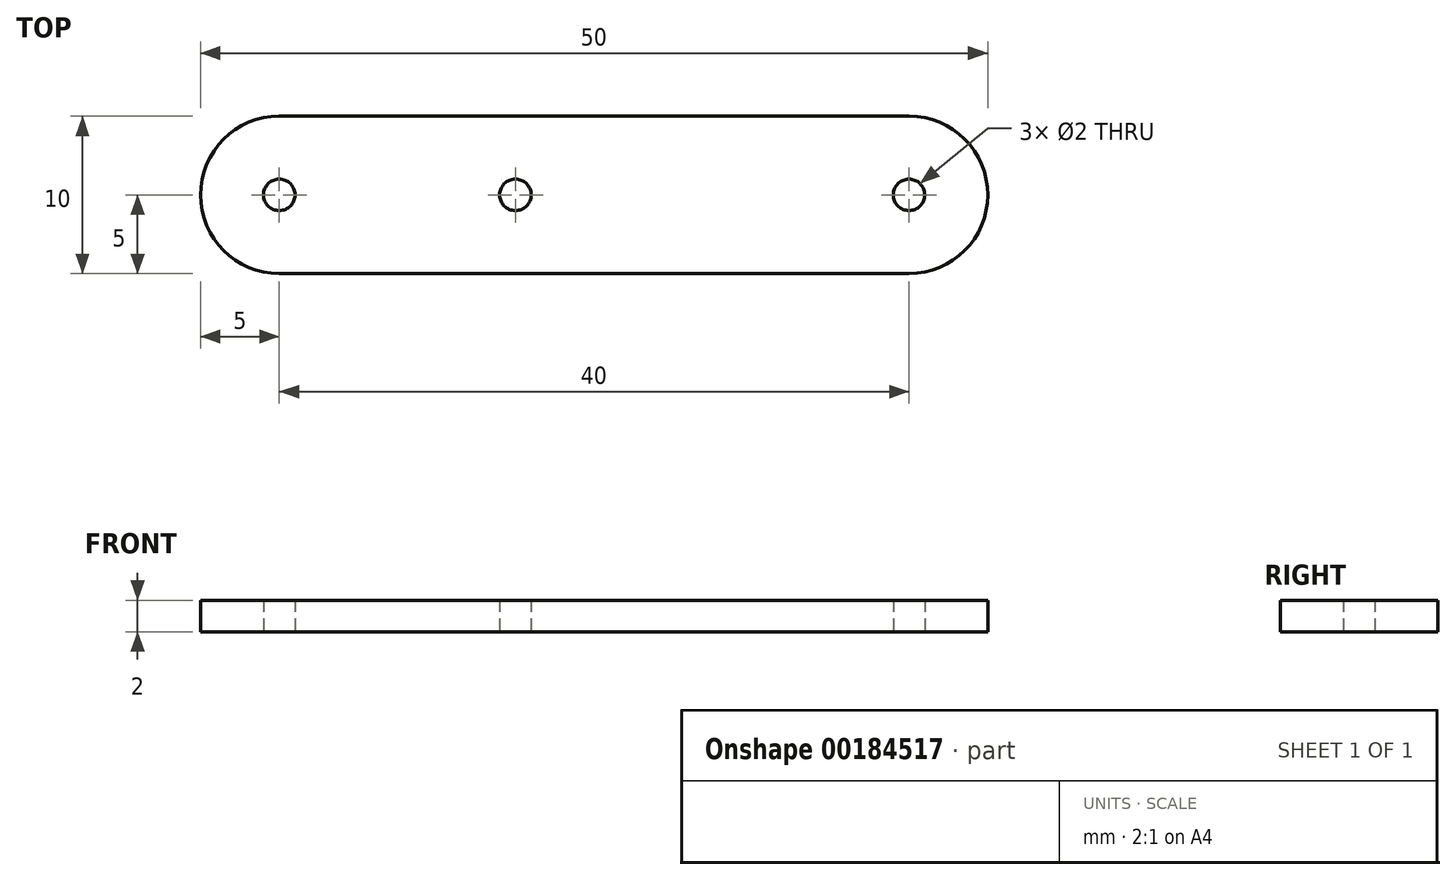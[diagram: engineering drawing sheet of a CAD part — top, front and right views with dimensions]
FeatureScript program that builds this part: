
annotation { "Feature Type Name" : "Feature", "Feature Type Description" : "" }
export const myFeature = defineFeature(function(context is Context, id is Id, definition is map)
    precondition{}
    {
        {
            var Q0;
            Q0=qCreatedBy(makeId("Top.planeOp"),FACE);
            var sketch = newSketch(context, id + "F0", { "sketchPlane" : qUnion([Q0])});
            skLineSegment(sketch, "E0.bottom", {"start": v(0, 0) * mm, "end": v(50, 0) * mm});
            skLineSegment(sketch, "E0.top", {"start": v(0, -10) * mm, "end": v(50, -10) * mm});
            skLineSegment(sketch, "E0.left", {"start": v(0, 0) * mm, "end": v(0, -10) * mm});
            skLineSegment(sketch, "E0.right", {"start": v(50, 0) * mm, "end": v(50, -10) * mm});
            skCircle(sketch, "E1", {"center": v(5, -5) * mm, "radius": 1 * mm});
            skCircle(sketch, "E2", {"center": v(20, -5) * mm, "radius": 1 * mm});
            skCircle(sketch, "E3", {"center": v(45, -5) * mm, "radius": 1 * mm});
            skSolve(sketch);
        }
        {
            var Q0;
            Q0=makeQuery(id+"F0.imprint","IMPRINT",FACE,{"disambiguationData":[TD([[makeQuery(id+"F0.imprint","IMPRINT",EDGE,{"derivedFrom":sQuery(id+"F0.wireOp",EDGE,"E0.bottom")}),-1.0]])]});
            extrude(context, id + "F1", {"entities" : qUnion([Q0]), "depth" : 2 * mm});
        }
        {
            var Q0;
            Q0=makeQuery(id+"F1.opExtrude","SWEPT_EDGE",EDGE,{"disambiguationData":[OSD([sQuery(id+"F0.wireOp",EDGE,"E0.bottom"),sQuery(id+"F0.wireOp",EDGE,"E0.left")])]});
            var Q1;
            Q1=makeQuery(id+"F1.opExtrude","SWEPT_EDGE",EDGE,{"disambiguationData":[OSD([sQuery(id+"F0.wireOp",EDGE,"E0.top"),sQuery(id+"F0.wireOp",EDGE,"E0.left")])]});
            var Q2;
            Q2=makeQuery(id+"F1.opExtrude","SWEPT_EDGE",EDGE,{"disambiguationData":[OSD([sQuery(id+"F0.wireOp",EDGE,"E0.bottom"),sQuery(id+"F0.wireOp",EDGE,"E0.right")])]});
            var Q3;
            Q3=makeQuery(id+"F1.opExtrude","SWEPT_EDGE",EDGE,{"disambiguationData":[OSD([sQuery(id+"F0.wireOp",EDGE,"E0.top"),sQuery(id+"F0.wireOp",EDGE,"E0.right")])]});
            fillet(context, id + "F2", {"entities" : qUnion([Q0, Q1, Q2, Q3]), "radius" : 5 * mm, "tangentPropagation" : true, "allowEdgeOverflow" : false});
        }
    });
